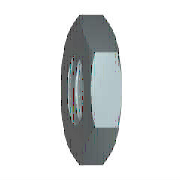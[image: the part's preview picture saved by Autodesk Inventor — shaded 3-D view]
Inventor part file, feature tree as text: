
AUTODESK INVENTOR PART (.ipt)
format: ipt  version: 2019 (Build 230136000, 136)  size: 165,888 bytes
history: native  units: mm (DEFAULTED — no unit token found)
features: sketch x3, chamfer x1, hole x1, other x1, plane x1
ambient origin geometry x7: Origin, YZ Plane, XZ Plane, X Axis, Y Axis, Z Axis, Center Point
bodies: Solid1 (feature_tree), Body (feature_tree)
feature tree (7):
  chamfer  "Chamfer1"  Angle=30.0deg  [1 undecoded]
  hole  "Thread"  [1 undecoded]
  other  "Work Axis1"
  plane  "Work Plane1"
  sketch  "Sketch1"  dims[d0=39.259818mm]
  sketch  "Sketch2"  dims[d1=11.0mm]
  sketch  "Sketch3"  dims[d2=0.0mm d3=30.0deg d4=30.0deg d5=31.35mm d6=31.35mm d7=90.0deg d25=20.376mm d26=6.0mm d27=4.0mm d28=2.0mm d29=14.3117mm d30=8.0mm d31=20.594885mm d8=0.811899mm d9=30.0deg d10=0.811899mm d11=30.0deg d13=0.0mm d14=0.0mm d39=0.0mm d40=0.811899mm d41=0.811899mm d42=0.0mm]
note: 2 required parameter values undecoded (feature->parameter linkage not recoverable at this tier; creation-order binding heuristic only, values carry confidence <= 0.55)
